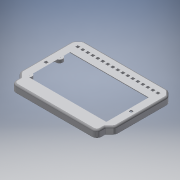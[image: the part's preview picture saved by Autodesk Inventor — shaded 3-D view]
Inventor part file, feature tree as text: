
AUTODESK INVENTOR PART (.ipt)
format: ipt  version: 2017 SP1 (Build 210196100, 196)  size: 1,597,440 bytes
history: native  units: mm
features: other x7, sketch x3, extrude x3, projected_geometry x2, reference x2, fillet x1, plane x1, chamfer x1, shell x1
ambient origin geometry x8: Origin, YZ Plane, XZ Plane, XY Plane, X Axis, Y Axis, Z Axis, Center Point
bodies: Volumenkörper1 (feature_tree), Volumenkörper3 (feature_tree)
feature tree (21):
  other  "GehäuseDeckel"
  other  "Deckel.ipt:1"
  other  "DummyAuschnitt2.ipt:1"
  fillet  "Rundung2"  Radius=10.0mm
  sketch  "Skizze6"  dims[d54=2.0mm d55=10.0mm d56=0.0mm]
  plane  "Arbeitsebene1"
  extrude  "Extrusion5"  Depth=10.0mm TaperAngle=0.0deg
  extrude  "Extrusion6"  Depth=1.0mm
  chamfer  "Fase2"  Distance=10.0mm
  extrude  "Extrusion8"  Depth=10.0mm
  shell  "Wandung1"  Thickness=1.0mm
  projected_geometry  "Projizierte Kontur6"
  reference  "Referenz3"
  sketch  "Skizze7"  dims[d57=1.73mm d58=1.0mm]
  projected_geometry  "Projizierte Kontur7"
  reference  "Referenz4"
  sketch  "Skizze11"  dims[d59=10.0mm d60=1.0mm d61=10.0mm d62=1.0mm d63=10.0mm d64=1.0mm d65=10.0mm d66=1.0mm d67=10.0mm d68=1.0mm d69=10.0mm d70=1.0mm d71=10.0mm d72=1.0mm d73=10.0mm d76=1.0mm d78=10.0mm d79=0.0mm d80=0.3mm d81=2.0mm d82=45.0deg d83=2.0mm d84=2.0mm d87=0.3mm d88=0.0mm d89=0.5mm]
  other  "<userpath>\Dropbox\Elektronik\aXe_Dashboard240XL\Gehäuse\Montiert.iam"
  other  "Montiert.iam"
  other  "PCB_SingleLedRow:1"
  other  "Schnittkanten projizieren2"
